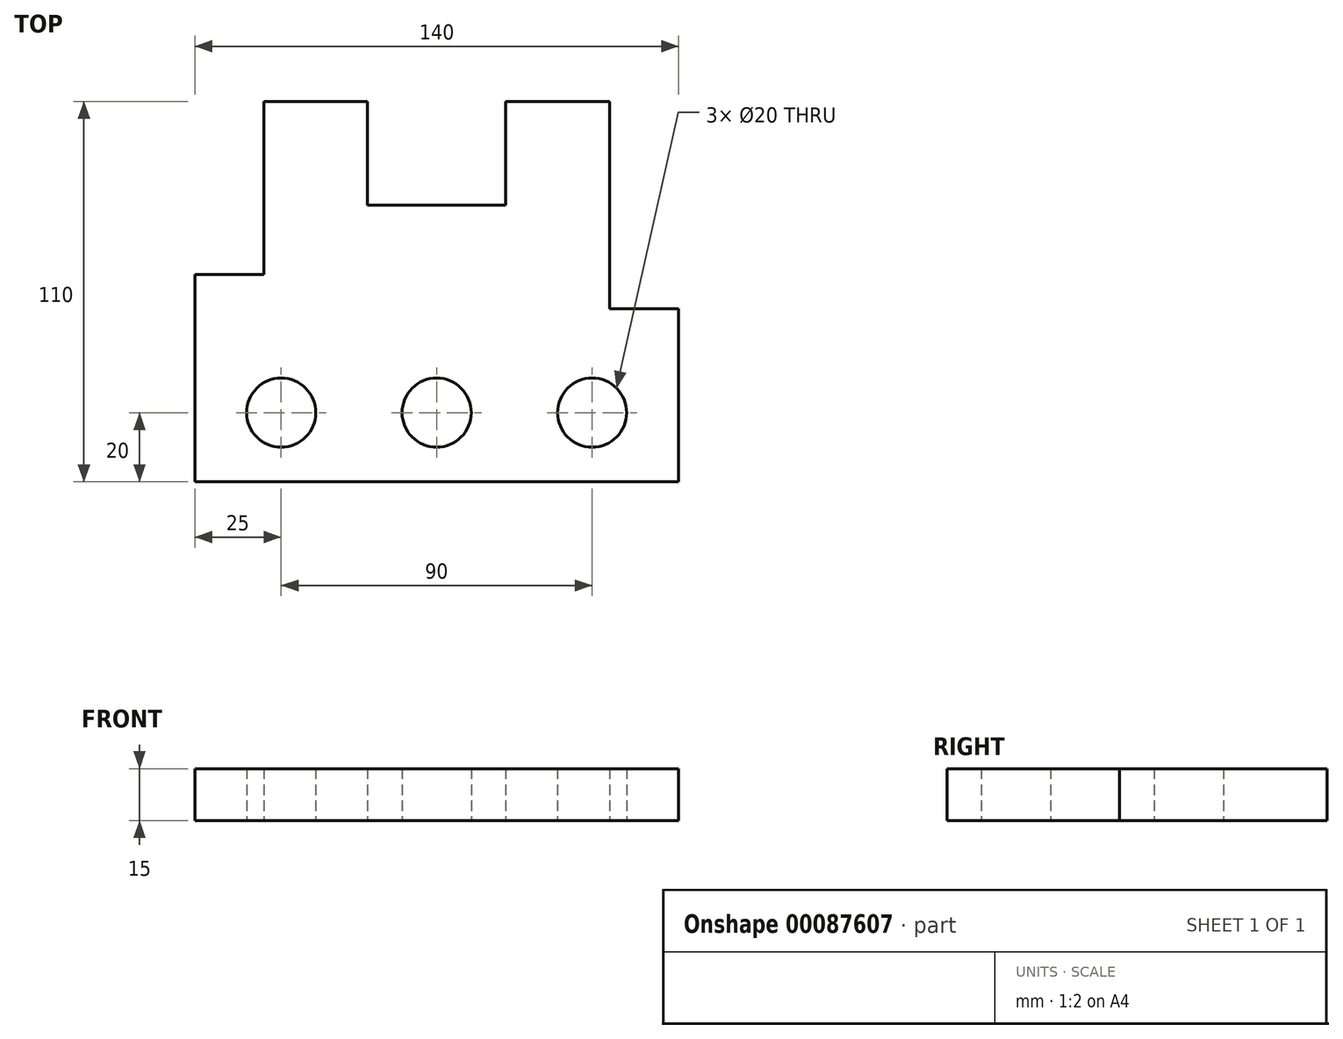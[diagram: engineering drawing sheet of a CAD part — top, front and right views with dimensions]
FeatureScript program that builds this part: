
annotation { "Feature Type Name" : "Feature", "Feature Type Description" : "" }
export const myFeature = defineFeature(function(context is Context, id is Id, definition is map)
    precondition{}
    {
        {
            var Q0;
            Q0=qCreatedBy(makeId("Top.planeOp"),FACE);
            var sketch = newSketch(context, id + "F0", { "sketchPlane" : qUnion([Q0])});
            skLineSegment(sketch, "E0.bottom", {"start": v(0, 0) * mm, "end": v(140, 0) * mm});
            skLineSegment(sketch, "E0.top", {"start": v(20, 110) * mm, "end": v(50, 110) * mm});
            skLineSegment(sketch, "E0.left", {"start": v(0, 0) * mm, "end": v(0, 60) * mm});
            skLineSegment(sketch, "E0.right", {"start": v(140, 0) * mm, "end": v(140, 50) * mm});
            skLineSegment(sketch, "E1.top", {"start": v(0, 60) * mm, "end": v(20, 60) * mm});
            skLineSegment(sketch, "E1.right", {"start": v(20, 110) * mm, "end": v(20, 60) * mm});
            skLineSegment(sketch, "E2.top", {"start": v(50, 80) * mm, "end": v(90, 80) * mm});
            skLineSegment(sketch, "E2.left", {"start": v(50, 110) * mm, "end": v(50, 80) * mm});
            skLineSegment(sketch, "E2.right", {"start": v(90, 110) * mm, "end": v(90, 80) * mm});
            skCircle(sketch, "E3", {"center": v(25, 20) * mm, "radius": 10 * mm});
            skCircle(sketch, "E4", {"center": v(70, 20) * mm, "radius": 10 * mm});
            skLineSegment(sketch, "E5", {"start": v(25, 20) * mm, "end": v(70, 20) * mm, "construction": true});
            skLineSegment(sketch, "E6", {"start": v(70, 20) * mm, "end": v(115, 20) * mm, "construction": true});
            skCircle(sketch, "E7", {"center": v(115, 20) * mm, "radius": 10 * mm});
            skLineSegment(sketch, "E8.trimOffspring", {"start": v(90, 110) * mm, "end": v(120, 110) * mm});
            skPoint(sketch, "E9.oppositeSnap0", {"position": v(120, 110) * mm});
            skLineSegment(sketch, "E9.top", {"start": v(140, 50) * mm, "end": v(120, 50) * mm});
            skLineSegment(sketch, "E9.right", {"start": v(120, 110) * mm, "end": v(120, 50) * mm});
            skSolve(sketch);
        }
        {
            var Q0;
            Q0 = qSketchRegion(id + "F0", true);
            extrude(context, id + "F1", {"entities" : qUnion([Q0]), "depth" : 15 * mm});
        }
    });
